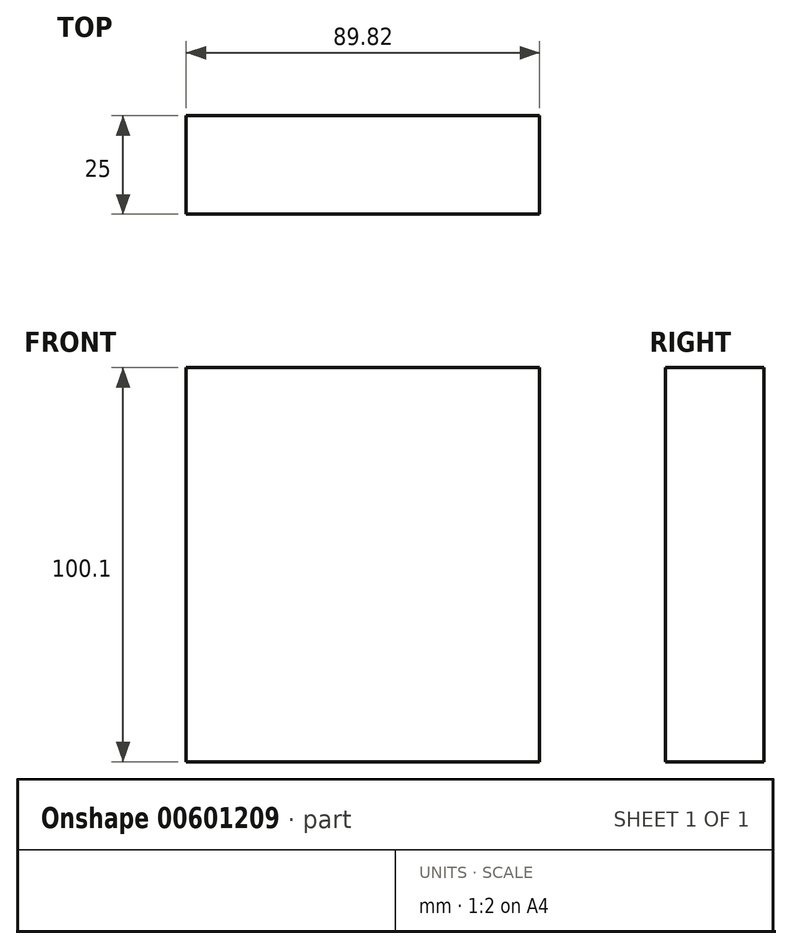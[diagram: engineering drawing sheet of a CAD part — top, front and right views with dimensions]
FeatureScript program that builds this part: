
annotation { "Feature Type Name" : "Feature", "Feature Type Description" : "" }
export const myFeature = defineFeature(function(context is Context, id is Id, definition is map)
    precondition{}
    {
        {
            var Q0;
            Q0=qCreatedBy(makeId("Front.planeOp"),FACE);
            var sketch = newSketch(context, id + "F0", { "sketchPlane" : qUnion([Q0])});
            skLineSegment(sketch, "E0.bottom", {"start": v(-115.9, 52.5) * mm, "end": v(-26.1, 52.5) * mm});
            skLineSegment(sketch, "E0.top", {"start": v(-115.9, -47.6) * mm, "end": v(-26.1, -47.6) * mm});
            skLineSegment(sketch, "E0.left", {"start": v(-115.9, 52.5) * mm, "end": v(-115.9, -47.6) * mm});
            skLineSegment(sketch, "E0.right", {"start": v(-26.1, 52.5) * mm, "end": v(-26.1, -47.6) * mm});
            skSolve(sketch);
        }
        {
            var Q0;
            Q0 = qSketchRegion(id + "F0", true);
            extrude(context, id + "F1", {"entities" : qUnion([Q0]), "depth" : 25 * mm, "offsetDistance" : 25 * mm});
        }
    });
